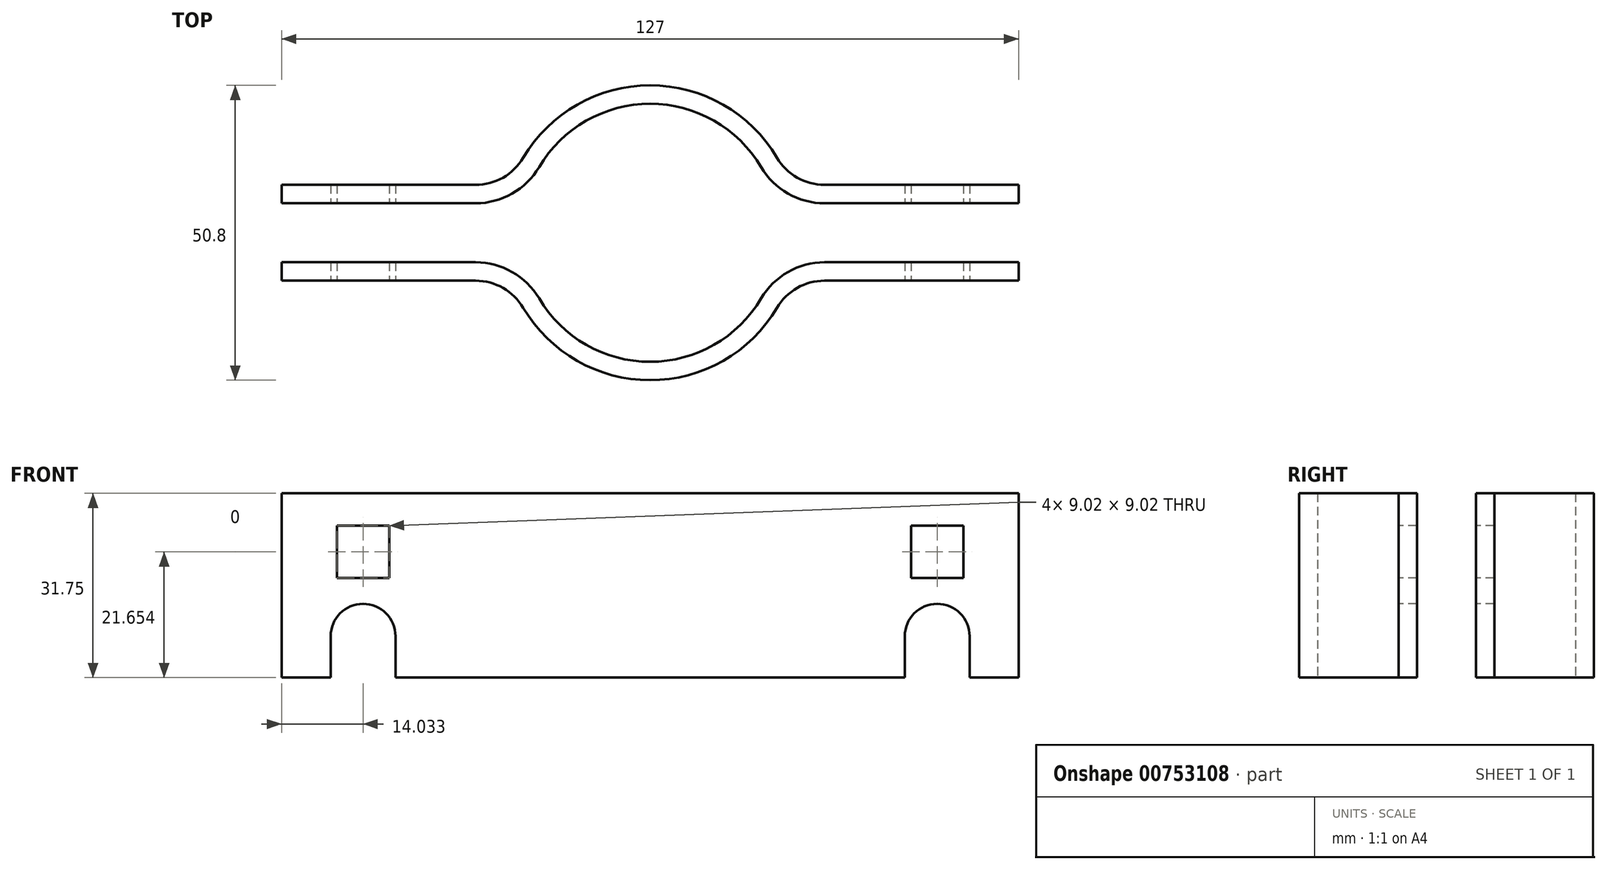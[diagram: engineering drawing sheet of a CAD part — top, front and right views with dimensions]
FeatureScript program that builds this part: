
annotation { "Feature Type Name" : "Feature", "Feature Type Description" : "" }
export const myFeature = defineFeature(function(context is Context, id is Id, definition is map)
    precondition{}
    {
        {
            var Q0;
            Q0=qCreatedBy(makeId("Top.planeOp"),FACE);
            var sketch = newSketch(context, id + "F0", { "sketchPlane" : qUnion([Q0])});
            skArc(sketch, "E0", {"start": v(-19.13, -11.31) * mm, "mid": v(0, -22.22) * mm, "end": v(19.13, -11.31) * mm});
            skLineSegment(sketch, "E1", {"start": v(-63.5, -5.08) * mm, "end": v(-30.06, -5.08) * mm});
            skLineSegment(sketch, "E2", {"start": v(-63.5, 8.25) * mm, "end": v(-63.5, 5.08) * mm});
            skLineSegment(sketch, "E3.MirrorCS", {"start": v(63.5, 8.26) * mm, "end": v(63.5, 5.08) * mm});
            skLineSegment(sketch, "E4.MirrorCS", {"start": v(-63.5, 5.08) * mm, "end": v(-30.06, 5.08) * mm});
            skArc(sketch, "E5.trimOffspring", {"start": v(19.13, 11.31) * mm, "mid": v(0, 22.23) * mm, "end": v(-19.13, 11.31) * mm});
            skLineSegment(sketch, "E6.trimOffspring", {"start": v(30.06, 5.08) * mm, "end": v(63.5, 5.08) * mm});
            skLineSegment(sketch, "E7.trimOffspring", {"start": v(30.06, -5.08) * mm, "end": v(63.5, -5.08) * mm});
            skPoint(sketch, "E8.visualSharp", {"position": v(21.64, -5.08) * mm});
            skArc(sketch, "E8.filletArc", {"start": v(30.06, -5.08) * mm, "mid": v(23.77, -6.75) * mm, "end": v(19.13, -11.31) * mm});
            skPoint(sketch, "E9.visualSharp", {"position": v(21.64, 5.08) * mm});
            skArc(sketch, "E9.filletArc", {"start": v(19.13, 11.31) * mm, "mid": v(23.77, 6.75) * mm, "end": v(30.06, 5.08) * mm});
            skPoint(sketch, "E10.visualSharp", {"position": v(-21.64, 5.08) * mm});
            skArc(sketch, "E10.filletArc", {"start": v(-30.06, 5.08) * mm, "mid": v(-23.77, 6.75) * mm, "end": v(-19.13, 11.31) * mm});
            skPoint(sketch, "E11.visualSharp", {"position": v(-21.64, -5.08) * mm});
            skArc(sketch, "E11.filletArc", {"start": v(-19.13, -11.31) * mm, "mid": v(-23.77, -6.75) * mm, "end": v(-30.06, -5.08) * mm});
            skLineSegment(sketch, "E12.0", {"start": v(-63.5, 8.25) * mm, "end": v(-30.06, 8.25) * mm});
            skArc(sketch, "E13.0", {"start": v(-30.06, 8.25) * mm, "mid": v(-25.34, 9.5) * mm, "end": v(-21.86, 12.93) * mm});
            skArc(sketch, "E14.0", {"start": v(21.86, 12.93) * mm, "mid": v(0, 25.4) * mm, "end": v(-21.86, 12.93) * mm});
            skArc(sketch, "E15.0", {"start": v(21.86, 12.93) * mm, "mid": v(25.34, 9.5) * mm, "end": v(30.06, 8.25) * mm});
            skLineSegment(sketch, "E16.0", {"start": v(30.06, 8.26) * mm, "end": v(63.5, 8.26) * mm});
            skLineSegment(sketch, "E17.trimOffspring", {"start": v(63.5, -5.08) * mm, "end": v(63.5, -8.26) * mm});
            skLineSegment(sketch, "E18.trimOffspring", {"start": v(-63.5, -5.08) * mm, "end": v(-63.5, -8.26) * mm});
            skLineSegment(sketch, "E19.0", {"start": v(30.06, -8.26) * mm, "end": v(63.5, -8.26) * mm});
            skLineSegment(sketch, "E19.1", {"start": v(-63.5, -8.26) * mm, "end": v(-30.06, -8.26) * mm});
            skArc(sketch, "E19.2", {"start": v(-21.86, -12.93) * mm, "mid": v(-25.34, -9.5) * mm, "end": v(-30.06, -8.26) * mm});
            skArc(sketch, "E19.3", {"start": v(-21.86, -12.93) * mm, "mid": v(0, -25.4) * mm, "end": v(21.86, -12.93) * mm});
            skArc(sketch, "E19.4", {"start": v(30.06, -8.26) * mm, "mid": v(25.34, -9.5) * mm, "end": v(21.86, -12.93) * mm});
            skSolve(sketch);
        }
        {
            var Q0;
            Q0=makeQuery(id+"F0.imprint","IMPRINT",FACE,{"disambiguationData":[TD([[makeQuery(id+"F0.imprint","IMPRINT",EDGE,{"derivedFrom":sQuery(id+"F0.wireOp",EDGE,"E0")}),-1.0]])]});
            var Q1;
            Q1=makeQuery(id+"F0.imprint","IMPRINT",FACE,{"disambiguationData":[TD([[makeQuery(id+"F0.imprint","IMPRINT",EDGE,{"derivedFrom":sQuery(id+"F0.wireOp",EDGE,"E2")}),1.0]])]});
            extrude(context, id + "F1", {"entities" : qUnion([Q0, Q1]), "depth" : 31.75 * mm, "offsetDistance" : 25.4 * mm});
        }
        {
            var Q0;
            Q0=qCreatedBy(makeId("Front.planeOp"),FACE);
            var sketch = newSketch(context, id + "F2", { "sketchPlane" : qUnion([Q0])});
            skLineSegment(sketch, "E20.0", {"start": v(-63.5, 31.75) * mm, "end": v(-63.5, 0) * mm});
            skLineSegment(sketch, "E21.0", {"start": v(-63.5, 31.75) * mm, "end": v(-30.06, 31.75) * mm});
            skLineSegment(sketch, "E22.trimOffspring", {"start": v(-53.98, 26.16) * mm, "end": v(-44.96, 26.16) * mm});
            skLineSegment(sketch, "E23.trimOffspring", {"start": v(-53.98, 26.16) * mm, "end": v(-53.98, 17.14) * mm});
            skLineSegment(sketch, "E24.trimOffspring", {"start": v(-44.96, 26.16) * mm, "end": v(-44.96, 17.14) * mm});
            skLineSegment(sketch, "E25.trimOffspring", {"start": v(-53.98, 17.14) * mm, "end": v(-44.96, 17.14) * mm});
            skArc(sketch, "E26", {"start": v(-43.88, 7.11) * mm, "mid": v(-49.47, 12.7) * mm, "end": v(-55.05, 7.11) * mm});
            skPoint(sketch, "E26.centerSnap0", {"position": v(-54, 7.11) * mm});
            skLineSegment(sketch, "E27", {"start": v(-55.05, 7.11) * mm, "end": v(-55.05, 0) * mm});
            skLineSegment(sketch, "E28", {"start": v(-43.88, 7.11) * mm, "end": v(-43.88, 0) * mm});
            skLineSegment(sketch, "E29.MirrorCS", {"start": v(53.98, 26.16) * mm, "end": v(53.98, 17.14) * mm});
            skLineSegment(sketch, "E30.MirrorCS", {"start": v(53.98, 26.16) * mm, "end": v(44.96, 26.16) * mm});
            skLineSegment(sketch, "E31.MirrorCS", {"start": v(44.96, 26.16) * mm, "end": v(44.96, 17.14) * mm});
            skLineSegment(sketch, "E32.MirrorCS", {"start": v(53.98, 17.14) * mm, "end": v(44.96, 17.14) * mm});
            skArc(sketch, "E33.MirrorCS", {"start": v(43.88, 7.11) * mm, "mid": v(49.47, 12.7) * mm, "end": v(55.05, 7.11) * mm});
            skLineSegment(sketch, "E34.MirrorCS", {"start": v(55.05, 7.11) * mm, "end": v(55.05, 0) * mm});
            skLineSegment(sketch, "E35.MirrorCS", {"start": v(43.88, 7.11) * mm, "end": v(43.88, 0) * mm});
            skLineSegment(sketch, "E36", {"start": v(-55.05, 0) * mm, "end": v(-43.88, 0) * mm});
            skLineSegment(sketch, "E37.MirrorCS", {"start": v(55.05, 0) * mm, "end": v(43.88, 0) * mm});
            skSolve(sketch);
        }
        {
            var Q0;
            Q0 = qSketchRegion(id + "F2", true);
            extrude(context, id + "F3", {"entities" : qUnion([Q0]), "operationType" : NewBodyOperationType.REMOVE, "endBound" : BoundingType.SYMMETRIC, "oppositeDirection" : true, "depth" : 50.8 * mm, "offsetDistance" : 25.4 * mm});
        }
    });
